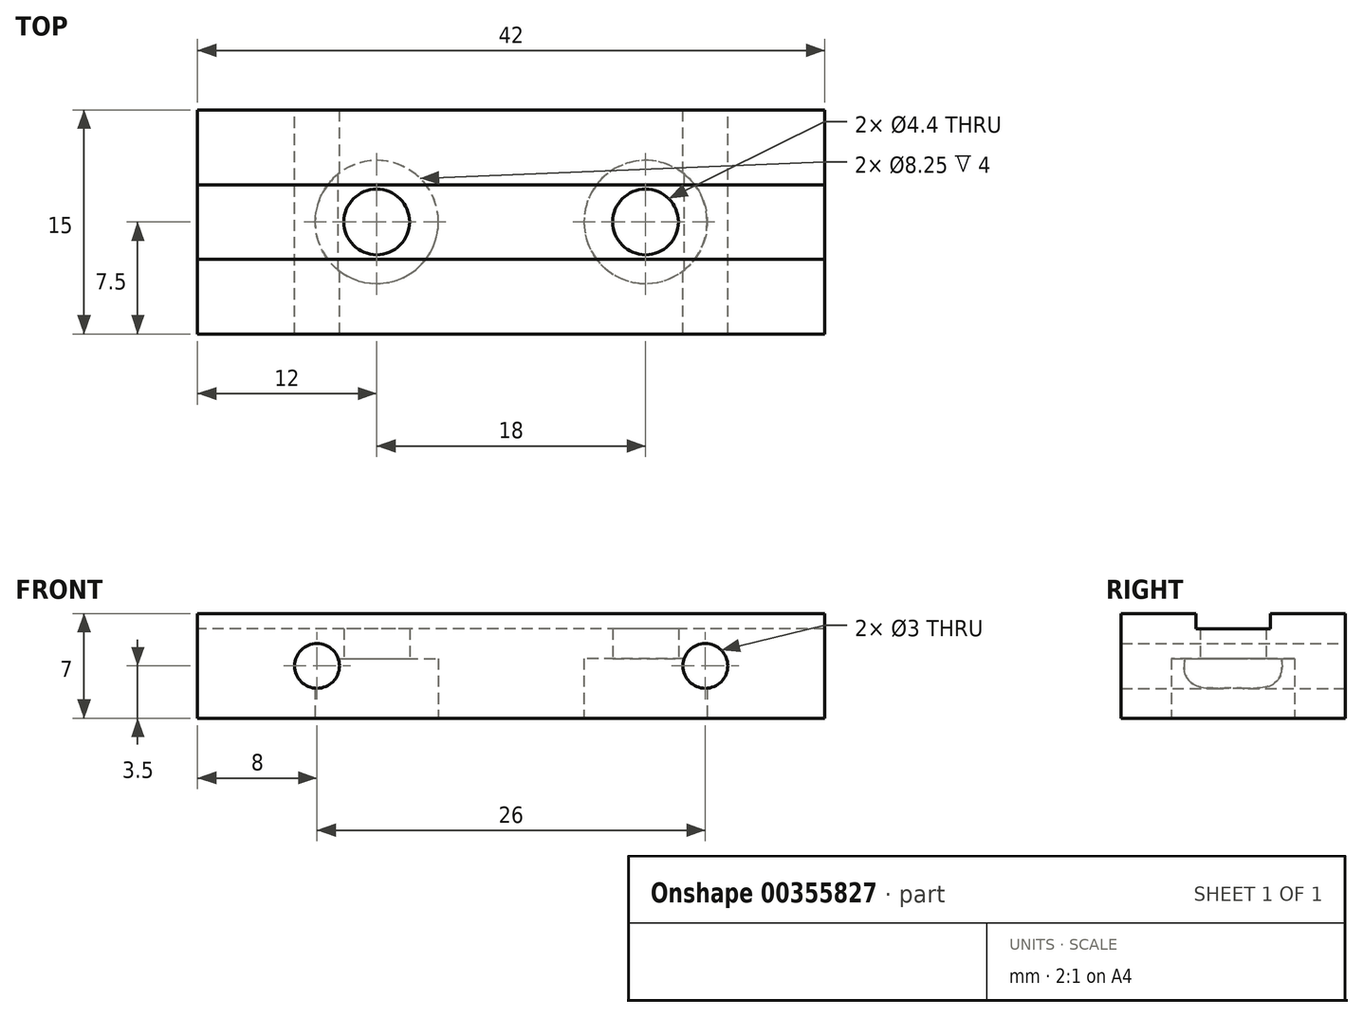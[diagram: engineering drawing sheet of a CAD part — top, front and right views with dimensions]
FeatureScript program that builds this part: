
annotation { "Feature Type Name" : "Feature", "Feature Type Description" : "" }
export const myFeature = defineFeature(function(context is Context, id is Id, definition is map)
    precondition{}
    {
        {
            var Q0;
            Q0=qCreatedBy(makeId("Top.planeOp"),FACE);
            var sketch = newSketch(context, id + "F0", { "sketchPlane" : qUnion([Q0])});
            skLineSegment(sketch, "E0.bottom", {"start": v(21, -7.5) * mm, "end": v(-21, -7.5) * mm});
            skLineSegment(sketch, "E0.top", {"start": v(21, 7.5) * mm, "end": v(-21, 7.5) * mm});
            skLineSegment(sketch, "E0.left", {"start": v(21, -7.5) * mm, "end": v(21, 7.5) * mm});
            skLineSegment(sketch, "E0.right", {"start": v(-21, -7.5) * mm, "end": v(-21, 7.5) * mm});
            skPoint(sketch, "E0.middle", {"position": v(0, 0) * mm});
            skSolve(sketch);
        }
        {
            var Q0;
            Q0=makeQuery(id+"F0.imprint","IMPRINT",FACE,{"disambiguationData":[TD([[makeQuery(id+"F0.imprint","IMPRINT",EDGE,{"derivedFrom":sQuery(id+"F0.wireOp",EDGE,"E0.bottom")}),-1.0]])]});
            extrude(context, id + "F1", {"entities" : qUnion([Q0]), "endBound" : BoundingType.SYMMETRIC, "depth" : 7 * mm});
        }
        {
            var Q0;
            Q0=makeQuery(id+"F1.opExtrude","CAP_FACE",FACE,{"disambiguationData":[OSD([sQuery(id+"F0.wireOp",EDGE,"E0.bottom"),sQuery(id+"F0.wireOp",EDGE,"E0.top"),sQuery(id+"F0.wireOp",EDGE,"E0.left"),sQuery(id+"F0.wireOp",EDGE,"E0.right")])],"isStart":false});
            var sketch = newSketch(context, id + "F2", { "sketchPlane" : qUnion([Q0])});
            skLineSegment(sketch, "E1.bottom", {"start": v(21, -2.5) * mm, "end": v(-21, -2.5) * mm});
            skLineSegment(sketch, "E1.top", {"start": v(21, 2.5) * mm, "end": v(-21, 2.5) * mm});
            skLineSegment(sketch, "E1.left", {"start": v(21, -2.5) * mm, "end": v(21, 2.5) * mm});
            skLineSegment(sketch, "E1.right", {"start": v(-21, -2.5) * mm, "end": v(-21, 2.5) * mm});
            skPoint(sketch, "E1.middle", {"position": v(0, 0) * mm});
            skSolve(sketch);
        }
        {
            var Q0;
            Q0=makeQuery(id+"F2.imprint","IMPRINT",FACE,{"disambiguationData":[TD([[makeQuery(id+"F2.imprint","IMPRINT",EDGE,{"derivedFrom":sQuery(id+"F2.wireOp",EDGE,"E1.bottom")}),-1.0]])]});
            extrude(context, id + "F3", {"entities" : qUnion([Q0]), "operationType" : NewBodyOperationType.REMOVE, "oppositeDirection" : true, "depth" : 1 * mm});
        }
        {
            var Q0;
            Q0=makeQuery(id+"F1.opExtrude","CAP_FACE",FACE,{"disambiguationData":[OSD([sQuery(id+"F0.wireOp",EDGE,"E0.bottom"),sQuery(id+"F0.wireOp",EDGE,"E0.top"),sQuery(id+"F0.wireOp",EDGE,"E0.left"),sQuery(id+"F0.wireOp",EDGE,"E0.right")])],"isStart":true});
            var sketch = newSketch(context, id + "F4", { "sketchPlane" : qUnion([Q0])});
            skCircle(sketch, "E2", {"center": v(9, 0) * mm, "radius": 2.97 * mm});
            skCircle(sketch, "E3", {"center": v(-9, 0) * mm, "radius": 3 * mm});
            skSolve(sketch);
        }
        {
            var Q0;
            Q0=sQuery(id+"F4.wireOp",VERTEX,"E2.center");
            var Q1;
            Q1=sQuery(id+"F4.wireOp",VERTEX,"E3.center");
            var Q2;
            Q2=makeQuery(id+"F1.opExtrude","SWEPT_BODY",BODY,{"disambiguationData":[OSD([sQuery(id+"F0.wireOp",EDGE,"E0.bottom"),sQuery(id+"F0.wireOp",EDGE,"E0.top"),sQuery(id+"F0.wireOp",EDGE,"E0.left"),sQuery(id+"F0.wireOp",EDGE,"E0.right")])]});
            hole(context, id + "F5", {"style" : HoleStyle.C_BORE, "endStyle" : HoleEndStyle.THROUGH, "standardTappedOrClearance" : lookupTablePath({ "standard" : "ISO", "fit" : "Normal", "size" : "M4", "type" : "Clearance" }), "standardBlindInLast" : lookupTablePath({ "fit" : "Standard", "standard" : "ISO", "size" : "M4", "type" : "Clearance" }), "holeDiameter" : 4.4 * mm, "cBoreDiameter" : 8.25 * mm, "cBoreDepth" : 4 * mm, "isTappedThrough" : true, "tappedDepth" : 12 * mm, "tapClearance" : 3, "startFromSketch" : true, "locations" : qUnion([Q0, Q1]), "scope" : qUnion([Q2])});
        }
        {
            var Q0;
            Q0=makeQuery(id+"F1.opExtrude","SWEPT_FACE",FACE,{"disambiguationData":[OSD([sQuery(id+"F0.wireOp",EDGE,"E0.top")])]});
            var sketch = newSketch(context, id + "F6", { "sketchPlane" : qUnion([Q0])});
            skCircle(sketch, "E4", {"center": v(-13, 0) * mm, "radius": 1.5 * mm});
            skCircle(sketch, "E5", {"center": v(13, 0) * mm, "radius": 1.5 * mm});
            skSolve(sketch);
        }
        {
            var Q0;
            Q0=makeQuery(id+"F6.imprint","IMPRINT",FACE,{"disambiguationData":[TD([[makeQuery(id+"F6.imprint","IMPRINT",EDGE,{"derivedFrom":sQuery(id+"F6.wireOp",EDGE,"E4")}),1.0]])]});
            var Q1;
            Q1=makeQuery(id+"F6.imprint","IMPRINT",FACE,{"disambiguationData":[TD([[makeQuery(id+"F6.imprint","IMPRINT",EDGE,{"derivedFrom":sQuery(id+"F6.wireOp",EDGE,"E5")}),1.0]])]});
            extrude(context, id + "F7", {"entities" : qUnion([Q0, Q1]), "operationType" : NewBodyOperationType.REMOVE, "endBound" : BoundingType.THROUGH_ALL, "oppositeDirection" : true, "depth" : 25 * mm});
        }
    });
